# Revit family: Hager-Univers-IP30-D160-Cl.II-FWQ-encl-AT-de
name_source: partatom
category: Equipement électrique
units: mm (PartAtom-declared; Revit-internal decimal feet)

## family parameters
Configuration du panneau = Deux colonnes, circuits au sein
Cote de connecteur circulaire = Utiliser le diamètre
Couper avec des vides une fois chargée = Non
Hôte = Face
Partagée = Non
Point de calcul de pièce = Non
Type d'élément = Tableau de raccordement

## types (13) — shared parameters
Commentaires du type = Univers
EF000003 - Montageart = EV000384 - Aufputz
EF000007 - Farbe = EV000202 - weiß
EF000049 - Tiefe = 160 mm  [stored 0.524934 ft]
EF000116 - RAL-Nummer = 9010
EF001088 - Anbaumöglichkeit = Oui
EF001596 - Werkstoff des Gehäuses = EV000179 - Stahl
EF001613 - Funktionserhalt = EV000494 - ohne
EF003532 - Geeignet für Außengebrauch = Non
EF005474 - Schutzart (IP) = EV006410 - IP30
EF006244 - Transparenter Deckel/Tür = Non
EF006306 - Mit Schloss = Non
EF007800 - Geeignet für Blitzschutz = Non
EF008873 - Nennstrom (In) = 125 A
EF009170 - Materialstärke Gehäuse = 2 mm  [stored 0.00656168 ft]
EF009171 - Materialstärke Tür/Deckel = 2 mm  [stored 0.00656168 ft]
EF009212 - Ausführung Deckel = EV009916 - mit Ausschnitt
EF015940 - Deckel mit Überdruckentlastung = Non
Fabricant = Hager
HG000002 - Mit tür = Non
HG000003 - Bereich = Univers
HG000006 - Unterputz = Non
HG000009 - Doppelflügeligen Tür = Non
HG000010 - Asymmetrische Türen = Non
HG000023 - Gehäuse mit doppeltem Querschnitt = Non
HG000024 - Höhe des unteren Teils = 800 mm  [stored 2.62467 ft]
HG000026 - Stehend auf dem Boden = Non
zero-valued in all types: EF000218 - Einbautiefe, Elévation par défaut, HG000027 - Sockelhöhe

## per-type parameters (varying)
| type | EF000008 - Breite | EF000040 - Höhe | EF000118 - Mit Montageplatte | EF000266 - Anzahl der Reihen | EF000339 - Art der Abdeckung | EF000437 - Anzahl der Leitungseinführungen | EF001131 - Innentiefe | EF002950 - Breite in Teilungseinheiten | EF004293 - Schlagfestigkeit | EF004427 - Anzahl der Module | EF004464 - Art der Tür | EF009554 - Anzahl der Öffnungen für Flanschplatten | HG000004 - Herstellerreferenz |
| Aufputz IP30 B1050 H650 T160  - FWQ34D1 | 1050 mm | 650 mm | Oui | 16 | EV001012 - Deckel | 16 | 160 mm  [stored 0.524934 ft] | 48 | EV006815 - IK09 | 192 | EV002646 - Einzel | 8 | FWQ34D1 |
| Aufputz IP30 B1050 H650 T160  - FWQ44D1 | 1050 mm | 650 mm | Oui | 16 | EV001012 - Deckel | 16 | 160 mm  [stored 0.524934 ft] | 48 |  | 192 | EV002646 - Einzel | 8 | FWQ44D1 |
| Aufputz IP30 B1050 H800 T160  - FWQ54D1 | 1050 mm | 800 mm  [stored 2.62467 ft] | Oui | 20 | EV001012 - Deckel | 16 | 160 mm  [stored 0.524934 ft] | 48 |  | 240 | EV002646 - Einzel | 8 | FWQ54D1 |
| Aufputz IP30 B300 H650 T160  - FWQ41D1 | 300 mm | 650 mm | Oui | 4 | EV001012 - Deckel | 4 | 160 mm  [stored 0.524934 ft] | 12 |  | 48 | EV002646 - Einzel | 2 | FWQ41D1 |
| Aufputz IP30 B300 H950 T160  - FWQ61D1 | 300 mm | 950 mm  [stored 3.1168 ft] | Oui | 6 | EV001012 - Deckel | 4 | 160 mm  [stored 0.524934 ft] | 12 |  | 72 | EV002646 - Einzel | 2 | FWQ61D1 |
| Aufputz IP30 B550 H1100 T160  - FWQ72D1 | 550 mm | 1100 mm | Oui | 14 | EV001012 - Deckel | 8 | 160 mm  [stored 0.524934 ft] | 12 |  | 168 | EV002646 - Einzel | 4 | FWQ72D1 |
| Aufputz IP30 B550 H650 T160  - FWQ42D1 | 550 mm | 650 mm | Oui | 8 | EV001012 - Deckel | 8 | 160 mm  [stored 0.524934 ft] | 24 |  | 96 | EV002646 - Einzel | 4 | FWQ42D1 |
| Aufputz IP30 B550 H800 T160  - FWQ52D1 | 550 mm | 800 mm  [stored 2.62467 ft] | Oui | 10 | EV001012 - Deckel | 8 | 160 mm  [stored 0.524934 ft] | 24 |  | 120 | EV002646 - Einzel | 4 | FWQ52D1 |
| Aufputz IP30 B550 H950 T160  - FWQ62D1 | 550 mm | 950 mm  [stored 3.1168 ft] | Oui | 12 | EV001012 - Deckel | 8 | 160 mm  [stored 0.524934 ft] | 24 |  | 144 | EV002646 - Einzel | 4 | FWQ62D1 |
| Aufputz IP30 B800 H500 T160  - FWQ33D1 | 800 mm  [stored 2.62467 ft] | 500 mm  [stored 1.64042 ft] | Non | 9 | EV000494 - ohne | 12 | 156 mm | 36 |  | 108 | EV000494 - ohne | 6 | FWQ33D1 |
| Aufputz IP30 B800 H650 T160  - FWQ43D1 | 800 mm  [stored 2.62467 ft] | 650 mm | Oui | 12 | EV001012 - Deckel | 12 | 160 mm  [stored 0.524934 ft] | 36 |  | 144 | EV002646 - Einzel | 6 | FWQ43D1 |
| Aufputz IP30 B800 H800 T160  - FWQ53D1 | 800 mm  [stored 2.62467 ft] | 800 mm  [stored 2.62467 ft] | Oui | 15 | EV001012 - Deckel | 12 | 160 mm  [stored 0.524934 ft] | 36 |  | 180 | EV002646 - Einzel | 6 | FWQ53D1 |
| Aufputz IP30 B800 H950 T160  - FWQ63D1 | 800 mm  [stored 2.62467 ft] | 950 mm  [stored 3.1168 ft] | Oui | 18 | EV001012 - Deckel | 12 | 160 mm  [stored 0.524934 ft] | 36 |  | 216 | EV002646 - Einzel | 6 | FWQ63D1 |

note: [stored X ft] marks values corroborated as IEEE doubles in the binary element streams (Revit-internal decimal feet)

## geometry (parser evidence)
native form markers: Sweep x10
no freeform markers — native parametric forms only
